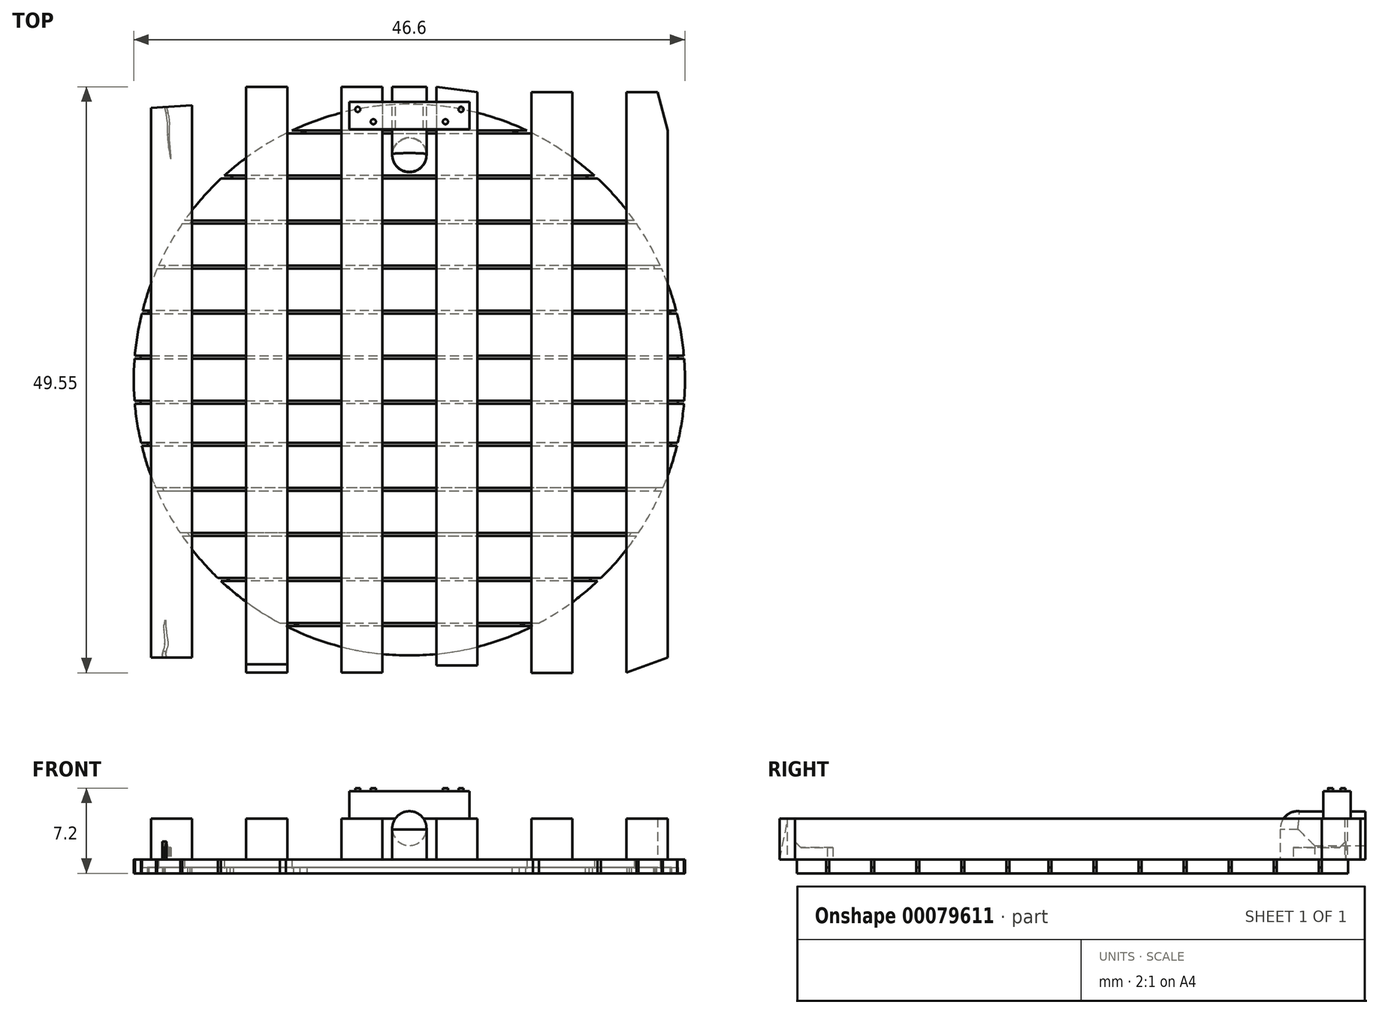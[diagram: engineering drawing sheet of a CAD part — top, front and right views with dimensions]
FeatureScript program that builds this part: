
annotation { "Feature Type Name" : "Feature", "Feature Type Description" : "" }
export const myFeature = defineFeature(function(context is Context, id is Id, definition is map)
    precondition{}
    {
        {
            var Q0;
            Q0=qCreatedBy(makeId("Top.planeOp"),FACE);
            var sketch = newSketch(context, id + "F0", { "sketchPlane" : qUnion([Q0])});
            skCircle(sketch, "E0", {"center": v(0, 0) * mm, "radius": 23.3 * mm});
            skSolve(sketch);
        }
        {
            var Q0;
            Q0 = qSketchRegion(id + "F0", true);
            extrude(context, id + "F1", {"entities" : qUnion([Q0]), "depth" : 1.16 * mm});
        }
        {
            var Q0;
            Q0=makeQuery(id+"F1.opExtrude","CAP_FACE",FACE,{"disambiguationData":[OSD([sQuery(id+"F0.wireOp",EDGE,"E0")])],"isStart":false});
            var sketch = newSketch(context, id + "F2", { "sketchPlane" : qUnion([Q0])});
            skLineSegment(sketch, "E1.bottom", {"start": v(-27.81, 1.78) * mm, "end": v(27.87, 1.78) * mm});
            skLineSegment(sketch, "E2", {"start": v(-27.81, 2.03) * mm, "end": v(27.87, 2.03) * mm});
            skLineSegment(sketch, "E3", {"start": v(-27.81, 5.59) * mm, "end": v(27.87, 5.59) * mm});
            skLineSegment(sketch, "E4", {"start": v(27.87, 5.84) * mm, "end": v(-27.81, 5.84) * mm});
            skLineSegment(sketch, "E5", {"start": v(-27.81, 9.4) * mm, "end": v(27.87, 9.4) * mm});
            skLineSegment(sketch, "E6", {"start": v(27.87, 9.65) * mm, "end": v(-27.81, 9.65) * mm});
            skLineSegment(sketch, "E7", {"start": v(-27.81, 13.2) * mm, "end": v(27.87, 13.2) * mm});
            skLineSegment(sketch, "E8", {"start": v(27.87, 13.46) * mm, "end": v(-27.81, 13.46) * mm});
            skLineSegment(sketch, "E9", {"start": v(-27.81, -1.78) * mm, "end": v(27.87, -1.78) * mm});
            skLineSegment(sketch, "E10", {"start": v(27.87, -5.33) * mm, "end": v(-27.81, -5.33) * mm});
            skLineSegment(sketch, "E11", {"start": v(-27.81, -5.59) * mm, "end": v(27.87, -5.59) * mm});
            skLineSegment(sketch, "E12", {"start": v(27.87, -9.14) * mm, "end": v(-27.81, -9.14) * mm});
            skLineSegment(sketch, "E13", {"start": v(27.87, -12.95) * mm, "end": v(-27.81, -12.95) * mm});
            skLineSegment(sketch, "E14", {"start": v(-27.81, -13.2) * mm, "end": v(27.87, -13.2) * mm});
            skLineSegment(sketch, "E15", {"start": v(27.87, 13.46) * mm, "end": v(27.87, 13.2) * mm});
            skLineSegment(sketch, "E16.trimOffspring", {"start": v(27.87, 9.65) * mm, "end": v(27.87, 9.4) * mm});
            skLineSegment(sketch, "E17.trimOffspring", {"start": v(27.87, -12.95) * mm, "end": v(27.87, -13.2) * mm});
            skLineSegment(sketch, "E18", {"start": v(-27.81, -9.4) * mm, "end": v(27.93, -9.4) * mm});
            skLineSegment(sketch, "E19", {"start": v(27.87, -9.14) * mm, "end": v(27.93, -9.4) * mm});
            skLineSegment(sketch, "E20.trimOffspring", {"start": v(27.87, -5.33) * mm, "end": v(27.87, -5.59) * mm});
            skLineSegment(sketch, "E21.trimOffspring", {"start": v(27.87, -1.78) * mm, "end": v(27.87, -2.03) * mm});
            skLineSegment(sketch, "E22.trimOffspring", {"start": v(27.87, 2.03) * mm, "end": v(27.87, 1.78) * mm});
            skLineSegment(sketch, "E23.trimOffspring", {"start": v(27.87, 5.84) * mm, "end": v(27.87, 5.59) * mm});
            skLineSegment(sketch, "E24", {"start": v(-27.81, 13.46) * mm, "end": v(-27.81, 13.2) * mm});
            skLineSegment(sketch, "E25.trimOffspring", {"start": v(-27.81, 9.65) * mm, "end": v(-27.81, 9.4) * mm});
            skLineSegment(sketch, "E26.trimOffspring", {"start": v(-27.81, 5.84) * mm, "end": v(-27.81, 5.59) * mm});
            skLineSegment(sketch, "E27.trimOffspring", {"start": v(-27.81, 2.03) * mm, "end": v(-27.81, 1.78) * mm});
            skLineSegment(sketch, "E28", {"start": v(27.87, -2.03) * mm, "end": v(-27.81, -2.03) * mm});
            skLineSegment(sketch, "E29.trimOffspring", {"start": v(-27.81, -1.78) * mm, "end": v(-27.81, -2.03) * mm});
            skLineSegment(sketch, "E30.trimOffspring", {"start": v(-27.81, -5.33) * mm, "end": v(-27.81, -5.59) * mm});
            skLineSegment(sketch, "E31.trimOffspring", {"start": v(-27.81, -9.14) * mm, "end": v(-27.81, -9.4) * mm});
            skLineSegment(sketch, "E32.trimOffspring", {"start": v(-27.81, -12.95) * mm, "end": v(-27.81, -13.2) * mm});
            skLineSegment(sketch, "E33", {"start": v(-21.28, 17.02) * mm, "end": v(23.62, 17.02) * mm});
            skLineSegment(sketch, "E34", {"start": v(23.62, 17.02) * mm, "end": v(23.68, 17.27) * mm});
            skLineSegment(sketch, "E35", {"start": v(23.68, 17.27) * mm, "end": v(-21.45, 17.27) * mm});
            skLineSegment(sketch, "E36", {"start": v(-21.45, 17.27) * mm, "end": v(-21.28, 17.02) * mm});
            skLineSegment(sketch, "E37", {"start": v(-18.64, 20.83) * mm, "end": v(26.06, 20.83) * mm});
            skLineSegment(sketch, "E38", {"start": v(26.06, 20.83) * mm, "end": v(26.06, 21.08) * mm});
            skLineSegment(sketch, "E39", {"start": v(26.06, 21.08) * mm, "end": v(-18.64, 21.08) * mm});
            skLineSegment(sketch, "E40", {"start": v(-18.64, 21.08) * mm, "end": v(-18.64, 20.83) * mm});
            skLineSegment(sketch, "E41", {"start": v(-27.81, -16.76) * mm, "end": v(27.87, -16.76) * mm});
            skLineSegment(sketch, "E42", {"start": v(27.87, -16.76) * mm, "end": v(27.87, -17.02) * mm});
            skLineSegment(sketch, "E43", {"start": v(27.87, -17.02) * mm, "end": v(-27.81, -17.02) * mm});
            skLineSegment(sketch, "E44", {"start": v(-27.81, -17.02) * mm, "end": v(-27.81, -16.76) * mm});
            skLineSegment(sketch, "E45", {"start": v(-27.81, -20.57) * mm, "end": v(27.77, -20.57) * mm});
            skLineSegment(sketch, "E46", {"start": v(27.77, -20.57) * mm, "end": v(27.77, -20.83) * mm});
            skLineSegment(sketch, "E47", {"start": v(27.77, -20.83) * mm, "end": v(-27.81, -20.83) * mm});
            skLineSegment(sketch, "E48", {"start": v(-27.81, -20.83) * mm, "end": v(-27.81, -20.57) * mm});
            skSolve(sketch);
        }
        {
            var Q0;
            Q0=makeQuery(id+"F1.opExtrude","CAP_FACE",FACE,{"disambiguationData":[OSD([sQuery(id+"F0.wireOp",EDGE,"E0")])],"isStart":false});
            var sketch = newSketch(context, id + "F3", { "sketchPlane" : qUnion([Q0])});
            skLineSegment(sketch, "E49.bottom", {"start": v(-5.76, 24.77) * mm, "end": v(-2.29, 24.77) * mm});
            skLineSegment(sketch, "E49.top", {"start": v(-5.76, -24.77) * mm, "end": v(-2.29, -24.77) * mm});
            skLineSegment(sketch, "E49.left", {"start": v(-5.76, 24.77) * mm, "end": v(-5.76, -24.77) * mm});
            skLineSegment(sketch, "E49.right", {"start": v(-2.29, 24.77) * mm, "end": v(-2.29, -24.77) * mm});
            skLineSegment(sketch, "E50.bottom", {"start": v(2.29, 24.77) * mm, "end": v(5.73, 24.33) * mm});
            skLineSegment(sketch, "E50.left", {"start": v(2.29, 24.77) * mm, "end": v(2.29, -24.15) * mm});
            skLineSegment(sketch, "E50.right", {"start": v(5.73, 24.33) * mm, "end": v(5.73, -24.15) * mm});
            skLineSegment(sketch, "E51.top", {"start": v(18.36, 24.33) * mm, "end": v(21, 24.33) * mm});
            skLineSegment(sketch, "E51.left", {"start": v(18.36, -24.77) * mm, "end": v(18.36, 24.33) * mm});
            skLineSegment(sketch, "E51.right", {"start": v(21.86, -23.48) * mm, "end": v(21.86, 21.09) * mm});
            skLineSegment(sketch, "E52.bottom", {"start": v(-10.33, 24.77) * mm, "end": v(-13.8, 24.77) * mm});
            skLineSegment(sketch, "E52.top", {"start": v(-10.33, -24.77) * mm, "end": v(-13.8, -24.77) * mm});
            skLineSegment(sketch, "E52.left", {"start": v(-10.33, 24.77) * mm, "end": v(-10.33, -24.77) * mm});
            skLineSegment(sketch, "E52.right", {"start": v(-13.8, 24.77) * mm, "end": v(-13.8, -24.77) * mm});
            skLineSegment(sketch, "E53.left", {"start": v(-18.38, -23.49) * mm, "end": v(-18.38, 23.23) * mm});
            skLineSegment(sketch, "E53.right", {"start": v(-21.85, -23.49) * mm, "end": v(-21.85, 23) * mm});
            skLineSegment(sketch, "E54", {"start": v(18.36, -24.77) * mm, "end": v(21.86, -23.48) * mm});
            skLineSegment(sketch, "E55", {"start": v(-21.85, -23.49) * mm, "end": v(-18.38, -23.49) * mm});
            skLineSegment(sketch, "E56", {"start": v(2.29, -24.15) * mm, "end": v(5.73, -24.15) * mm});
            skPoint(sketch, "E57.orphan", {"position": v(-18.38, -24.77) * mm});
            skPoint(sketch, "E58.orphan", {"position": v(5.73, -24.77) * mm});
            skLineSegment(sketch, "E59", {"start": v(-21.85, 23) * mm, "end": v(-18.38, 23.23) * mm});
            skPoint(sketch, "E60.orphan", {"position": v(-21.85, 24.77) * mm});
            skLineSegment(sketch, "E61", {"start": v(21, 24.33) * mm, "end": v(21.86, 21.09) * mm});
            skPoint(sketch, "E62.orphan", {"position": v(21.86, 24.33) * mm});
            skLineSegment(sketch, "E63.bottom", {"start": v(10.3, 24.33) * mm, "end": v(13.79, 24.33) * mm});
            skLineSegment(sketch, "E63.top", {"start": v(10.3, -24.78) * mm, "end": v(13.79, -24.78) * mm});
            skLineSegment(sketch, "E63.left", {"start": v(10.3, 24.33) * mm, "end": v(10.3, -24.78) * mm});
            skLineSegment(sketch, "E63.right", {"start": v(13.79, 24.33) * mm, "end": v(13.79, -24.78) * mm});
            skSolve(sketch);
        }
        {
            var Q0;
            Q0 = qSketchRegion(id + "F3", true);
            extrude(context, id + "F4", {"entities" : qUnion([Q0]), "operationType" : NewBodyOperationType.ADD, "depth" : 3.47 * mm});
        }
        {
            var Q0;
            Q0 = qSketchRegion(id + "F2", true);
            extrude(context, id + "F5", {"entities" : qUnion([Q0]), "operationType" : NewBodyOperationType.REMOVE, "oppositeDirection" : true, "depth" : 25.4 * mm});
        }
        {
            var Q0;
            {var subQ0=sQuery(id+"F0.wireOp",EDGE,"E0");Q0=makeQuery(id+"F5.boolean.opBoolean","SPLIT",FACE,{"disambiguationData":[TD([makeQuery(id+"F5.opExtrude","SWEPT_FACE",FACE,{"disambiguationData":[OSD([sQuery(id+"F2.wireOp",EDGE,"E11")])]})])],"derivedFrom":makeQuery(id+"F1.opExtrude","CAP_FACE",FACE,{"disambiguationData":[OSD([subQ0])],"isStart":true})});}
            var sketch = newSketch(context, id + "F6", { "sketchPlane" : qUnion([Q0])});
            skCircle(sketch, "E64", {"center": v(0, 0) * mm, "radius": 22.8 * mm});
            skSolve(sketch);
        }
        {
            var Q0;
            Q0 = qSketchRegion(id + "F6", true);
            extrude(context, id + "F7", {"entities" : qUnion([Q0]), "operationType" : NewBodyOperationType.ADD, "oppositeDirection" : true, "depth" : 0.5 * mm});
        }
        {
            var Q0;
            Q0=makeQuery(id+"F4.opExtrude","SWEPT_FACE",FACE,{"disambiguationData":[OSD([sQuery(id+"F3.wireOp",EDGE,"E52.left")])]});
            var sketch = newSketch(context, id + "F8", { "sketchPlane" : qUnion([Q0])});
            skLineSegment(sketch, "E65", {"start": v(-24.77, 1.16) * mm, "end": v(-24.06, 4.63) * mm});
            skLineSegment(sketch, "E66", {"start": v(-24.06, 4.63) * mm, "end": v(-24.77, 4.63) * mm});
            skLineSegment(sketch, "E67", {"start": v(-24.77, 4.63) * mm, "end": v(-24.77, 1.16) * mm});
            skSolve(sketch);
        }
        {
            var Q0;
            Q0 = qSketchRegion(id + "F8", true);
            extrude(context, id + "F9", {"entities" : qUnion([Q0]), "operationType" : NewBodyOperationType.REMOVE, "oppositeDirection" : true, "depth" : 5.08 * mm});
        }
        {
            var Q0;
            {var subQ0=sQuery(id+"F3.wireOp",EDGE,"E53.left");var subQ2=sQuery(id+"F3.wireOp",EDGE,"E53.right");var subQ3=sQuery(id+"F3.wireOp",EDGE,"E55");Q0=makeQuery(id+"F5.boolean.opBoolean","MERGE",FACE,{"derivedFrom":[makeQuery(id+"F4.boolean.opBoolean","SPLIT",FACE,{"disambiguationData":[TD([makeQuery(id+"F4.opExtrude","SWEPT_FACE",FACE,{"disambiguationData":[OSD([subQ3])]})])],"derivedFrom":makeQuery(id+"F4.opExtrude","CAP_FACE",FACE,{"disambiguationData":[OSD([subQ0,subQ2,subQ3,sQuery(id+"F3.wireOp",EDGE,"E59")])],"isStart":true})}),makeQuery(id+"F5.opExtrude","CAP_FACE",FACE,{"disambiguationData":[OSD([sQuery(id+"F2.wireOp",EDGE,"E12"),sQuery(id+"F2.wireOp",EDGE,"E18"),sQuery(id+"F2.wireOp",EDGE,"E19"),sQuery(id+"F2.wireOp",EDGE,"E31.trimOffspring")])],"isStart":true}),makeQuery(id+"F5.opExtrude","CAP_FACE",FACE,{"disambiguationData":[OSD([sQuery(id+"F2.wireOp",EDGE,"E13"),sQuery(id+"F2.wireOp",EDGE,"E14"),sQuery(id+"F2.wireOp",EDGE,"E17.trimOffspring"),sQuery(id+"F2.wireOp",EDGE,"E32.trimOffspring")])],"isStart":true})]});}
            var sketch = newSketch(context, id + "F10", { "sketchPlane" : qUnion([Q0])});
            skFitSpline(sketch, "E68", {"points": [v(-20.83, 23.72) * mm, v(-20.84, 23.04) * mm, v(-20.67, 22.25) * mm, v(-20.76, 20.74) * mm, v(-20.74, 20.74) * mm, v(-20.63, 20.28) * mm, v(-20.55, 21.28) * mm, v(-20.42, 22.45) * mm, v(-20.6, 23.1) * mm, v(-20.56, 23.72) * mm, v(-20.83, 23.72) * mm]});
            skFitSpline(sketch, "E69", {"points": [v(-20.9, -23.82) * mm, v(-20.58, -22.48) * mm, v(-20.42, -20.15) * mm, v(-20.16, -18.66) * mm, v(-20.29, -20.72) * mm, v(-20.27, -21.72) * mm, v(-20.6, -23.26) * mm, v(-20.9, -23.82) * mm]});
            skSolve(sketch);
        }
        {
            var Q0;
            Q0 = qSketchRegion(id + "F10", true);
            extrude(context, id + "F11", {"entities" : qUnion([Q0]), "operationType" : NewBodyOperationType.REMOVE, "oppositeDirection" : true, "depth" : 1.02 * mm});
        }
        {
            var Q0;
            Q0=makeQuery(id+"F11.boolean.opBoolean","INTERSECT",EDGE,{"derivedFrom":[makeQuery(id+"F4.opExtrude","SWEPT_FACE",FACE,{"disambiguationData":[OSD([sQuery(id+"F3.wireOp",EDGE,"E55")])]}),makeQuery(id+"F11.opExtrude","CAP_FACE",FACE,{"disambiguationData":[OSD([sQuery(id+"F10.wireOp",EDGE,"E68")])],"isStart":false})]});
            var Q1;
            Q1=makeQuery(id+"F11.boolean.opBoolean","INTERSECT",EDGE,{"derivedFrom":[makeQuery(id+"F4.opExtrude","SWEPT_FACE",FACE,{"disambiguationData":[OSD([sQuery(id+"F3.wireOp",EDGE,"E59")])]}),makeQuery(id+"F11.opExtrude","CAP_FACE",FACE,{"disambiguationData":[OSD([sQuery(id+"F10.wireOp",EDGE,"E69")])],"isStart":false})]});
            chamfer(context, id + "F12", {"entities" : qUnion([Q0, Q1]), "width" : 0.5 * mm, "tangentPropagation" : true});
        }
        {
            var Q0;
            {var subQ2=sQuery(id+"F3.wireOp",EDGE,"E49.right");var subQ3=makeQuery(id+"F4.opExtrude","SWEPT_FACE",FACE,{"disambiguationData":[OSD([subQ2])]});var subQ4=sQuery(id+"F2.wireOp",EDGE,"E39");var subQ6=sQuery(id+"F0.wireOp",EDGE,"E0");Q0=makeQuery(id+"F5.boolean.opBoolean","SPLIT",FACE,{"disambiguationData":[TD([makeQuery(id+"F5.opExtrude","SWEPT_FACE",FACE,{"disambiguationData":[OSD([subQ4])]})])],"derivedFrom":makeQuery(id+"F4.boolean.opBoolean","SPLIT",FACE,{"disambiguationData":[TD([subQ3])],"derivedFrom":makeQuery(id+"F1.opExtrude","CAP_FACE",FACE,{"disambiguationData":[OSD([subQ6])],"isStart":false})})});}
            var sketch = newSketch(context, id + "F13", { "sketchPlane" : qUnion([Q0])});
            skCircle(sketch, "E70", {"center": v(0, 19) * mm, "radius": 1.45 * mm});
            skSolve(sketch);
        }
        {
            var Q0;
            Q0 = qSketchRegion(id + "F13", true);
            extrude(context, id + "F14", {"entities" : qUnion([Q0]), "operationType" : NewBodyOperationType.ADD, "depth" : 2.54 * mm});
        }
        {
            var Q0;
            Q0=qCreatedBy(makeId("Right.planeOp"),FACE);
            var sketch = newSketch(context, id + "F15", { "sketchPlane" : qUnion([Q0])});
            skArc(sketch, "E71", {"start": v(19.03, 5.25) * mm, "mid": v(17.58, 3.8) * mm, "end": v(19.03, 2.35) * mm});
            skLineSegment(sketch, "E72", {"start": v(19.03, 2.35) * mm, "end": v(19.03, 5.25) * mm});
            skSolve(sketch);
        }
        {
            var Q0;
            Q0=makeQuery(id+"F15.imprint","IMPRINT",FACE,{"disambiguationData":[TD([[makeQuery(id+"F15.imprint","IMPRINT",EDGE,{"derivedFrom":sQuery(id+"F15.wireOp",EDGE,"E71")}),1.0]])]});
            var Q1;
            Q1=sQuery(id+"F15.wireOp",EDGE,"E71");
            var Q2;
            Q2=sQuery(id+"F15.wireOp",EDGE,"E72");
            revolve(context, id + "F16", {"operationType" : NewBodyOperationType.ADD, "entities" : qUnion([Q0]), "surfaceEntities" : qUnion([Q1]), "axis" : qUnion([Q2]), "revolveType" : RevolveType.FULL});
        }
        {
            var Q0;
            Q0=makeQuery(id+"F4.opExtrude","SWEPT_FACE",FACE,{"disambiguationData":[OSD([sQuery(id+"F3.wireOp",EDGE,"E49.bottom")])]});
            var sketch = newSketch(context, id + "F17", { "sketchPlane" : qUnion([Q0])});
            skCircle(sketch, "E73", {"center": v(0, 3.8) * mm, "radius": 1.45 * mm});
            skSolve(sketch);
        }
        {
            var Q0;
            Q0 = qSketchRegion(id + "F17", true);
            extrude(context, id + "F18", {"entities" : qUnion([Q0]), "operationType" : NewBodyOperationType.ADD, "oppositeDirection" : true, "depth" : 5.7 * mm});
        }
        {
            var Q0;
            Q0=makeQuery(id+"F4.opExtrude","CAP_FACE",FACE,{"disambiguationData":[OSD([sQuery(id+"F3.wireOp",EDGE,"E49.bottom"),sQuery(id+"F3.wireOp",EDGE,"E49.top"),sQuery(id+"F3.wireOp",EDGE,"E49.left"),sQuery(id+"F3.wireOp",EDGE,"E49.right")])],"isStart":false});
            var sketch = newSketch(context, id + "F19", { "sketchPlane" : qUnion([Q0])});
            skLineSegment(sketch, "E74.bottom", {"start": v(-5.08, 23.5) * mm, "end": v(5.08, 23.5) * mm});
            skLineSegment(sketch, "E74.top", {"start": v(-5.08, 21.19) * mm, "end": v(5.08, 21.19) * mm});
            skLineSegment(sketch, "E74.left", {"start": v(-5.08, 23.5) * mm, "end": v(-5.08, 21.19) * mm});
            skLineSegment(sketch, "E74.right", {"start": v(5.08, 23.5) * mm, "end": v(5.08, 21.19) * mm});
            skSolve(sketch);
        }
        {
            var Q0;
            Q0 = qSketchRegion(id + "F19", true);
            extrude(context, id + "F20", {"entities" : qUnion([Q0]), "operationType" : NewBodyOperationType.ADD, "depth" : 2.31 * mm});
        }
        {
            var Q0;
            Q0=makeQuery(id+"F20.opExtrude","CAP_FACE",FACE,{"disambiguationData":[OSD([sQuery(id+"F19.wireOp",EDGE,"E74.bottom"),sQuery(id+"F19.wireOp",EDGE,"E74.top"),sQuery(id+"F19.wireOp",EDGE,"E74.left"),sQuery(id+"F19.wireOp",EDGE,"E74.right")])],"isStart":false});
            var sketch = newSketch(context, id + "F21", { "sketchPlane" : qUnion([Q0])});
            skCircle(sketch, "E75", {"center": v(-4.37, 22.87) * mm, "radius": 0.22 * mm});
            skCircle(sketch, "E76", {"center": v(-3.05, 21.83) * mm, "radius": 0.22 * mm});
            skCircle(sketch, "E77", {"center": v(4.37, 22.87) * mm, "radius": 0.22 * mm});
            skCircle(sketch, "E78", {"center": v(3.05, 21.83) * mm, "radius": 0.22 * mm});
            skSolve(sketch);
        }
        {
            var Q0;
            Q0 = qSketchRegion(id + "F21", true);
            extrude(context, id + "F22", {"entities" : qUnion([Q0]), "operationType" : NewBodyOperationType.ADD, "depth" : 0.25 * mm});
        }
    });
